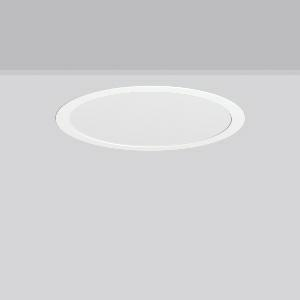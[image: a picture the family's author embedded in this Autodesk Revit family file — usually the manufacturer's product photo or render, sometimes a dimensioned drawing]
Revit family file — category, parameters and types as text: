
# Revit family: toledo_flat__round_e_901810_002_76_c6f4
name_source: partatom
category: Lighting Fixtures
units: mm (PartAtom-declared; Revit-internal decimal feet)

## family parameters
Cut with Voids When Loaded = No
Host = Face
Light Source = No
Part Type = Normal
Room Calculation Point = No
Round Connector Dimension = Use Diameter
Shared = No

## types (1)
- MultiLumen 1 (1 x LED Modul 840, 1550 lm, 4000)
    Apparent Load = 12 VA
    CIE Flux Codes = 47 79 96 100 100
    Color Rendering = 80
    Color Temperature = 4000
    Default Elevation = 1800 mm
    Description = Series: TOLEDO FLAT+ round
Flexible round recessed multifunction downlight. Housing: sheet steel, powder-coated. Luminaire frame: aluminium, powder-coated. Light guide and diffuser made of non-yellowing PMMA, opal matt. LED backlight technology for homogeneous illumination of the entire light-emitting surface. MultiColour: Colour temperature individually adjustable either 3000 K or 4000 K via switching element. Factory setting is 4000 K. MultiLumen: 4 steps adjustable luminous flux. Factory setting is step 2. Suitable for Recessed ceiling mounting. Ceiling installation with spring system. Can be directly covered with thermal insulation material (applies only to the lower lumen levels). Including separate LED converter with connecting cable 250 mm. Suitable for through wiring as standard. Surface mounted housing as accessory for all sizes. 
Colour: white
Diameter: 390 mm
Height: 2 mm
Cut-out diameter: 377 mm
Recess height: 60 mm
Luminaire: recess height: 40 mm
Lamp: LED
Socket: without socket
Colour temperature: 3000K, 4000K
Colour rendering index (CRI): 80
System power: 12 W
Rated luminous flux: 1550 lm
Luminous efficiency: 129 lm/W
System power 2: 15 W
Rated luminous flux 2: 2050 lm
Luminous efficiency 2: 137 lm/W
System power 3: 19 W
Rated luminous flux 3: 2550 lm
Luminous efficiency 3: 134 lm/W
System power 4: 22 W
Rated luminous flux 4: 2950 lm
Luminous efficiency 4: 134 lm/W
Control gear: Converter, dimmable, DALI
Protection class: II
Type of protection: IP 54
    Height = 0 mm  [stored 0 ft]
    Lamp = 1 x LED Modul 840
    Lamp Light Flux = 1550 lm
    Lamp count = 1
    Length = 390 mm
    Lifetime = 50000 h
    Luminous efficacy = 129 lm/W
    Manufacturer = RZB
    ModVariant = No
    Model = 901810.002.76
    Mounting Place = Ceiling
    Mounting Type = Recessed
    Number of Poles = 1
    OnlyDefault = Yes
    Power Factor = 1
    Product Name = TOLEDO FLAT+ round E
    Product group = Recessed downlights
    ProductGroupID = 402
    Protection Class = Protection class II
    Protection Degree = Degree of protection
    RLX_Detail_Level = 1
    RLX_Emergency_Light_Flux = 0 lm
    RLX_Emergency_Type = 0
    RLX_Emergency_Type_DB = No
    RlxData = <blob elided: 34225 chars, md5=3bca638a>
    Socket = socket
    Standby Power = 0 W
    System Light Flux = 1550 lm
    System Power = 12 W
    Type Comments = MultiLumen 1
    Type Image = 901810.002.jpg
    URL = http://relux.com
    VarID = multilumen_1
    Voltage = 0 V
    Weight = 0.00 kg
    Width = 0 mm  [stored 0 ft]

note: [stored X ft] marks values corroborated as IEEE doubles in the binary element streams (Revit-internal decimal feet)

## geometry (parser evidence)
native form markers: Blend x4, Sweep x10
no freeform markers — native parametric forms only
